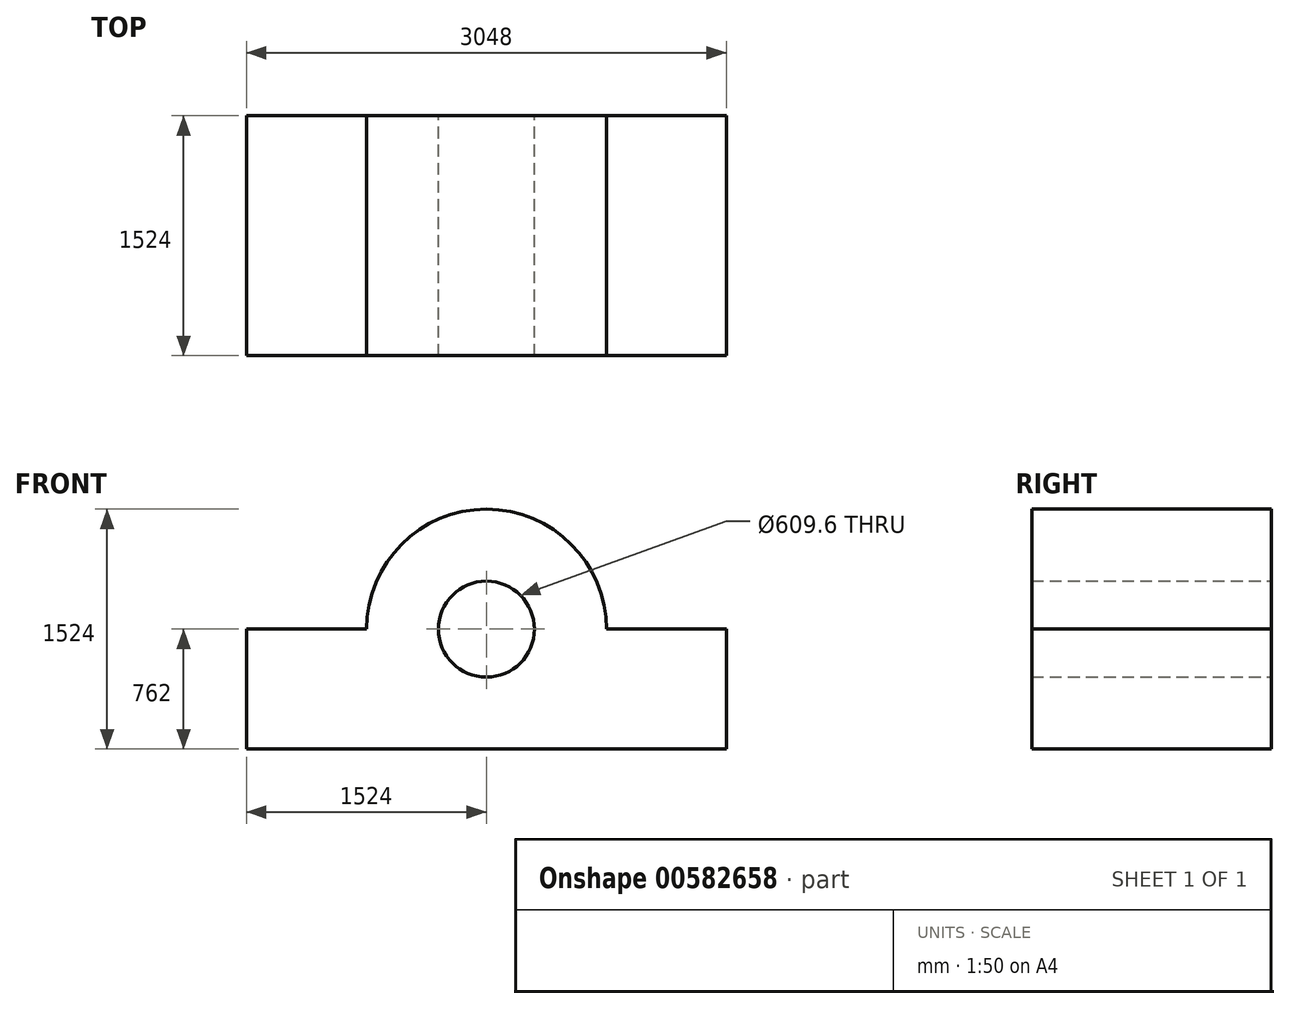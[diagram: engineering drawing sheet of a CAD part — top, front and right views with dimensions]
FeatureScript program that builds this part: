
annotation { "Feature Type Name" : "Feature", "Feature Type Description" : "" }
export const myFeature = defineFeature(function(context is Context, id is Id, definition is map)
    precondition{}
    {
        {
            var Q0;
            Q0=qCreatedBy(makeId("Front.planeOp"),FACE);
            var sketch = newSketch(context, id + "F0", { "sketchPlane" : qUnion([Q0])});
            skLineSegment(sketch, "E0", {"start": v(0, 0) * mm, "end": v(3048, 0) * mm});
            skLineSegment(sketch, "E1", {"start": v(3048, 0) * mm, "end": v(3048, 762) * mm});
            skLineSegment(sketch, "E2", {"start": v(0, 0) * mm, "end": v(0, 762) * mm});
            skLineSegment(sketch, "E3", {"start": v(0, 762) * mm, "end": v(762, 762) * mm});
            skLineSegment(sketch, "E4", {"start": v(3048, 762) * mm, "end": v(2286, 762) * mm});
            skCircle(sketch, "E5", {"center": v(1524, 762) * mm, "radius": 304.8 * mm});
            skPoint(sketch, "E5.centerSnap0", {"position": v(1524, 0) * mm});
            skArc(sketch, "E6", {"start": v(2286, 762) * mm, "mid": v(1524, 1524) * mm, "end": v(762, 762) * mm});
            skSolve(sketch);
        }
        {
            var Q0;
            Q0 = qSketchRegion(id + "F0", true);
            extrude(context, id + "F1", {"entities" : qUnion([Q0]), "depth" : 1524 * mm, "offsetDistance" : 25.4 * mm});
        }
    });
